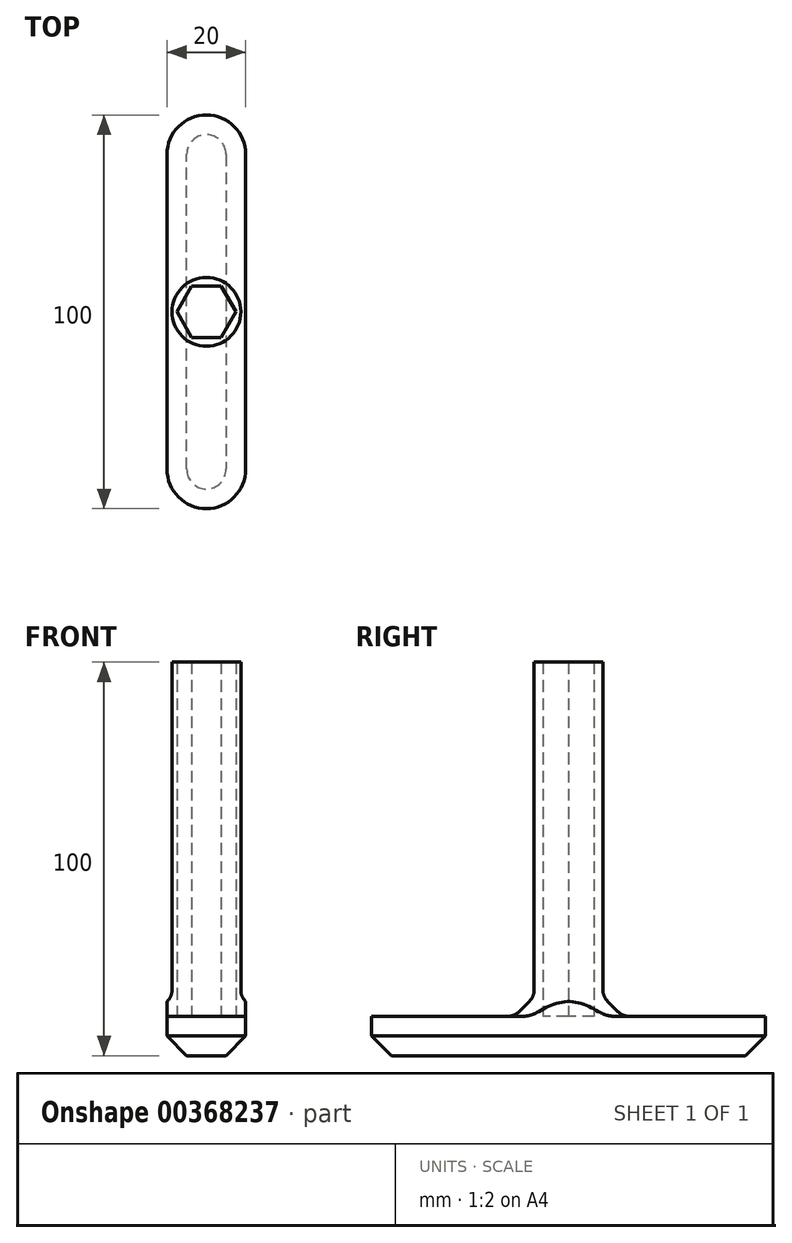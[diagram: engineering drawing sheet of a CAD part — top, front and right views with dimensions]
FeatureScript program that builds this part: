
annotation { "Feature Type Name" : "Feature", "Feature Type Description" : "" }
export const myFeature = defineFeature(function(context is Context, id is Id, definition is map)
    precondition{}
    {
        {
            var Q0;
            Q0=qCreatedBy(makeId("Top.planeOp"),FACE);
            var sketch = newSketch(context, id + "F0", { "sketchPlane" : qUnion([Q0])});
            skCircle(sketch, "E0", {"center": v(0, 0) * mm, "radius": 8.75 * mm});
            skCircle(sketch, "E1.cCircle", {"center": v(0, 0) * mm, "radius": 7.5 * mm, "construction": true});
            skLineSegment(sketch, "E1.0", {"start": v(7.5, 0) * mm, "end": v(3.75, -6.5) * mm});
            skLineSegment(sketch, "E1.1", {"start": v(3.75, -6.5) * mm, "end": v(-3.75, -6.5) * mm});
            skLineSegment(sketch, "E1.2", {"start": v(-3.75, -6.5) * mm, "end": v(-7.5, 0) * mm});
            skLineSegment(sketch, "E1.3", {"start": v(-7.5, 0) * mm, "end": v(-3.75, 6.5) * mm});
            skLineSegment(sketch, "E1.4", {"start": v(-3.75, 6.5) * mm, "end": v(3.75, 6.5) * mm});
            skLineSegment(sketch, "E1.5", {"start": v(3.75, 6.5) * mm, "end": v(7.5, 0) * mm});
            skSolve(sketch);
        }
        {
            var Q0;
            Q0 = qSketchRegion(id + "F0", true);
            extrude(context, id + "F1", {"entities" : qUnion([Q0]), "depth" : 90 * mm});
        }
        {
            var Q0;
            Q0=qCreatedBy(makeId("Top.planeOp"),FACE);
            var sketch = newSketch(context, id + "F2", { "sketchPlane" : qUnion([Q0])});
            skLineSegment(sketch, "E2", {"start": v(0, 0) * mm, "end": v(0, 40) * mm, "construction": true});
            skLineSegment(sketch, "E3", {"start": v(0, 0) * mm, "end": v(0, -40) * mm, "construction": true});
            skArc(sketch, "E4.0.endCap", {"start": v(-10, 40) * mm, "mid": v(0, 50) * mm, "end": v(10, 40) * mm});
            skLineSegment(sketch, "E4.0.left", {"start": v(-10, 0) * mm, "end": v(-10, 40) * mm});
            skLineSegment(sketch, "E4.0.right", {"start": v(10, 0) * mm, "end": v(10, 40) * mm});
            skArc(sketch, "E5.0.endCap", {"start": v(10, -40) * mm, "mid": v(0, -50) * mm, "end": v(-10, -40) * mm});
            skLineSegment(sketch, "E5.0.left", {"start": v(10, 0) * mm, "end": v(10, -40) * mm});
            skLineSegment(sketch, "E5.0.right", {"start": v(-10, 0) * mm, "end": v(-10, -40) * mm});
            skSolve(sketch);
        }
        {
            var Q0;
            Q0 = qSketchRegion(id + "F2", true);
            extrude(context, id + "F3", {"entities" : qUnion([Q0]), "operationType" : NewBodyOperationType.ADD, "oppositeDirection" : true, "depth" : 10 * mm});
        }
        {
            var Q0;
            Q0=makeQuery(id+"F1.opExtrude","CAP_EDGE",EDGE,{"disambiguationData":[OSD([sQuery(id+"F0.wireOp",EDGE,"E0")])],"isStart":true});
            chamfer(context, id + "F4", {"entities" : qUnion([Q0]), "width" : 5 * mm, "tangentPropagation" : true});
        }
        {
            var Q0;
            {var subQ0=sQuery(id+"F2.wireOp",EDGE,"E5.0.left");var subQ1=sQuery(id+"F2.wireOp",EDGE,"E4.0.right");var subQ2=sQuery(id+"F2.wireOp",EDGE,"E5.0.right");var subQ3=sQuery(id+"F2.wireOp",EDGE,"E4.0.left");var subQ4=sQuery(id+"F2.wireOp",EDGE,"E4.0.endCap");var subQ5=sQuery(id+"F0.wireOp",EDGE,"E0");var subQ6=sQuery(id+"F2.wireOp",EDGE,"E5.0.endCap");Q0=makeQuery(id+"F4.opChamfer","BLEND_EDGE",EDGE,{"disambiguationData":[OD(0.0)],"blendedFrom":[makeQuery(id+"F1.opExtrude","CAP_EDGE",EDGE,{"disambiguationData":[OSD([subQ5])],"isStart":true}),makeQuery(id+"F3.boolean.opBoolean","SPLIT",FACE,{"disambiguationData":[TD([makeQuery(id+"F1.opExtrude","SWEPT_FACE",FACE,{"disambiguationData":[OSD([subQ5])]})])],"derivedFrom":makeQuery(id+"F3.opExtrude","CAP_FACE",FACE,{"disambiguationData":[OSD([subQ4,subQ3,subQ1,subQ6,subQ0,subQ2])],"isStart":true})})],"blendedInto":[makeQuery(id+"F3.boolean.opBoolean","SPLIT",FACE,{"disambiguationData":[TD([makeQuery(id+"F1.opExtrude","SWEPT_FACE",FACE,{"disambiguationData":[OSD([subQ5])]})])],"derivedFrom":makeQuery(id+"F3.opExtrude","CAP_FACE",FACE,{"disambiguationData":[OSD([subQ4,subQ3,subQ1,subQ6,subQ0,subQ2])],"isStart":true})})]});}
            var Q1;
            {var subQ0=sQuery(id+"F2.wireOp",EDGE,"E5.0.left");var subQ1=sQuery(id+"F2.wireOp",EDGE,"E4.0.right");var subQ2=sQuery(id+"F2.wireOp",EDGE,"E5.0.right");var subQ3=sQuery(id+"F2.wireOp",EDGE,"E4.0.left");var subQ4=sQuery(id+"F2.wireOp",EDGE,"E4.0.endCap");var subQ5=sQuery(id+"F0.wireOp",EDGE,"E0");var subQ6=sQuery(id+"F2.wireOp",EDGE,"E5.0.endCap");Q1=makeQuery(id+"F4.opChamfer","BLEND_EDGE",EDGE,{"disambiguationData":[OD(1.0)],"blendedFrom":[makeQuery(id+"F1.opExtrude","CAP_EDGE",EDGE,{"disambiguationData":[OSD([subQ5])],"isStart":true}),makeQuery(id+"F3.boolean.opBoolean","SPLIT",FACE,{"disambiguationData":[TD([makeQuery(id+"F1.opExtrude","SWEPT_FACE",FACE,{"disambiguationData":[OSD([subQ5])]})])],"derivedFrom":makeQuery(id+"F3.opExtrude","CAP_FACE",FACE,{"disambiguationData":[OSD([subQ4,subQ3,subQ1,subQ6,subQ0,subQ2])],"isStart":true})})],"blendedInto":[makeQuery(id+"F3.boolean.opBoolean","SPLIT",FACE,{"disambiguationData":[TD([makeQuery(id+"F1.opExtrude","SWEPT_FACE",FACE,{"disambiguationData":[OSD([subQ5])]})])],"derivedFrom":makeQuery(id+"F3.opExtrude","CAP_FACE",FACE,{"disambiguationData":[OSD([subQ4,subQ3,subQ1,subQ6,subQ0,subQ2])],"isStart":true})})]});}
            var Q2;
            {var subQ0=sQuery(id+"F0.wireOp",EDGE,"E0");Q2=makeQuery(id+"F4.opChamfer","BLEND_EDGE",EDGE,{"blendedFrom":[makeQuery(id+"F1.opExtrude","CAP_EDGE",EDGE,{"disambiguationData":[OSD([subQ0])],"isStart":true}),makeQuery(id+"F1.opExtrude","SWEPT_FACE",FACE,{"disambiguationData":[OSD([subQ0])]})],"blendedInto":[makeQuery(id+"F1.opExtrude","SWEPT_FACE",FACE,{"disambiguationData":[OSD([subQ0])]})]});}
            fillet(context, id + "F5", {"entities" : qUnion([Q0, Q1, Q2]), "radius" : 4 * mm, "tangentPropagation" : true, "allowEdgeOverflow" : false});
        }
        {
            var Q0;
            Q0=makeQuery(id+"F3.opExtrude","CAP_EDGE",EDGE,{"disambiguationData":[OSD([sQuery(id+"F2.wireOp",EDGE,"E4.0.right"),sQuery(id+"F2.wireOp",EDGE,"E5.0.left")])],"isStart":false});
            chamfer(context, id + "F6", {"entities" : qUnion([Q0]), "width" : 5 * mm, "tangentPropagation" : true});
        }
    });
